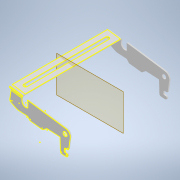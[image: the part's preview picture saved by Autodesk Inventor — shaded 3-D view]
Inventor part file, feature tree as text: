
AUTODESK INVENTOR PART (.ipt)
format: ipt  version: 2022 (Build 260153000, 153)  size: 489,472 bytes
history: native  units: mm
features: other x25, reference x18, sketch x8, projected_geometry x4, mirror x2, fillet x1
ambient origin geometry x8: Origin, YZ Plane, XZ Plane, XY Plane, X Axis, Y Axis, Z Axis, Center Point
bodies: Body1 (feature_tree)
feature tree (58):
  other  "Твердое тело1"
  other  "Грань1"
  other  "Фланец1"
  other  "УглСкругление1"
  other  "УглСкругление2"
  other  "УглСкругление3"
  other  "УглСкругление4"
  other  "УглСкругление5"
  mirror  "Зеркальное отражение1"
  other  "Грань2"
  other  "РабПлоскость1"
  mirror  "Зеркальное отражение2"
  other  "УглСкругление9"
  other  "УглСкругление10"
  fillet  "Сопряжение1"  Radius=1.0mm
  other  "Определение главной стороны"
  sketch  "Эскиз7"
  sketch  "Эскиз8"
  sketch  "Эскиз1"
  reference  "Ссылка1"
  reference  "Ссылка2"
  reference  "Ссылка3"
  reference  "Ссылка4"
  reference  "Ссылка8"
  reference  "Ссылка9"
  reference  "Ссылка10"
  reference  "Ссылка11"
  other  "Пластина1"
  reference  "Ссылка12"
  reference  "Ссылка13"
  reference  "Ссылка16"
  sketch  "Эскиз2"
  other  "Пластина2"
  other  "Сгиб1"
  other  "УглСтык1"
  reference  "Ссылка17"
  sketch  "Эскиз3"
  projected_geometry  "Спроецированная петля1"
  sketch  "Эскиз4"
  projected_geometry  "Спроецированная петля3"
  reference  "Ссылка22"
  sketch  "Эскиз5"
  reference  "Ссылка23"
  reference  "Ссылка24"
  reference  "Ссылка25"
  reference  "Ссылка26"
  reference  "Ссылка27"
  other  "Пластина3"
  other  "Сгиб2"
  sketch  "Эскиз6"
  projected_geometry  "Спроецированная петля4"
  projected_geometry  "Спроецированная петля5"
  other  "Вырез1"
  other  "Вырез2"
  other  "Вырез3"
  other  "<userpath>\Documents\Git\MZCAT_battery\FastBattery.iam"
  other  "FastBattery.iam"
  other  "akkum_base1:1"
